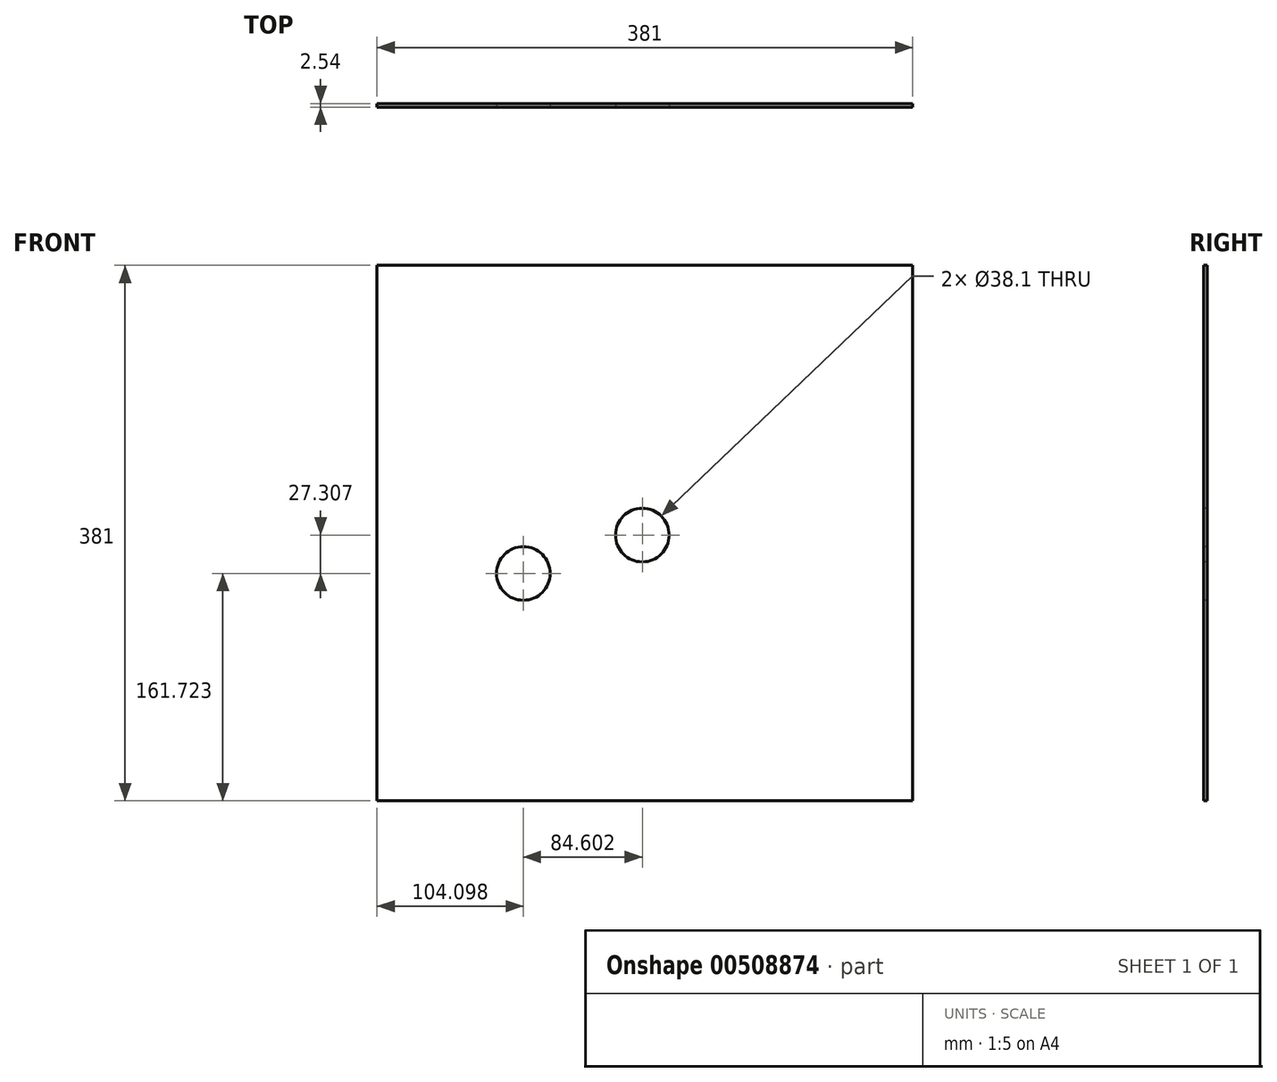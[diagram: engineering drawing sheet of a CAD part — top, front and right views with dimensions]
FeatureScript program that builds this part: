
annotation { "Feature Type Name" : "Feature", "Feature Type Description" : "" }
export const myFeature = defineFeature(function(context is Context, id is Id, definition is map)
    precondition{}
    {
        {
            var Q0;
            Q0=qCreatedBy(makeId("Front.planeOp"),FACE);
            var sketch = newSketch(context, id + "F0", { "sketchPlane" : qUnion([Q0])});
            skLineSegment(sketch, "E0.bottom", {"start": v(-188.7, 191.97) * mm, "end": v(192.3, 191.97) * mm});
            skLineSegment(sketch, "E0.top", {"start": v(-188.7, -189.03) * mm, "end": v(192.3, -189.03) * mm});
            skLineSegment(sketch, "E0.left", {"start": v(-188.7, 191.97) * mm, "end": v(-188.7, -189.03) * mm});
            skLineSegment(sketch, "E0.right", {"start": v(192.3, 191.97) * mm, "end": v(192.3, -189.03) * mm});
            skSolve(sketch);
        }
        {
            var Q0;
            Q0=makeQuery(id+"F0.imprint","IMPRINT",FACE,{"disambiguationData":[TD([[makeQuery(id+"F0.imprint","IMPRINT",EDGE,{"derivedFrom":sQuery(id+"F0.wireOp",EDGE,"E0.bottom")}),-1.0]])]});
            extrude(context, id + "F1", {"entities" : qUnion([Q0]), "depth" : 2.54 * mm});
        }
        {
            var Q0;
            Q0=makeQuery(id+"F1.opExtrude","CAP_FACE",FACE,{"disambiguationData":[OSD([sQuery(id+"F0.wireOp",EDGE,"E0.bottom"),sQuery(id+"F0.wireOp",EDGE,"E0.top"),sQuery(id+"F0.wireOp",EDGE,"E0.left"),sQuery(id+"F0.wireOp",EDGE,"E0.right")])],"isStart":false});
            var sketch = newSketch(context, id + "F2", { "sketchPlane" : qUnion([Q0])});
            skArc(sketch, "E1", {"start": v(85.58, 148.56) * mm, "mid": v(165.63, -44.3) * mm, "end": v(0, -171.45) * mm});
            skCircle(sketch, "E2", {"center": v(0, 0) * mm, "radius": 50.8 * mm, "construction": true});
            skLineSegment(sketch, "E3", {"start": v(85.58, 148.56) * mm, "end": v(-103.68, 257.6) * mm});
            skLineSegment(sketch, "E4", {"start": v(0, -171.45) * mm, "end": v(-323.77, -171.45) * mm});
            skCircle(sketch, "E5", {"center": v(0, 0) * mm, "radius": 19.05 * mm});
            skCircle(sketch, "E6", {"center": v(-84.6, -27.3) * mm, "radius": 19.05 * mm});
            skSolve(sketch);
        }
        {
            var Q0;
            Q0=qSketchRegion(id+"F2",true);
            extrude(context, id + "F3", {"entities" : qUnion([Q0]), "operationType" : NewBodyOperationType.REMOVE, "endBound" : BoundingType.THROUGH_ALL, "oppositeDirection" : true, "depth" : 25.4 * mm});
        }
    });
